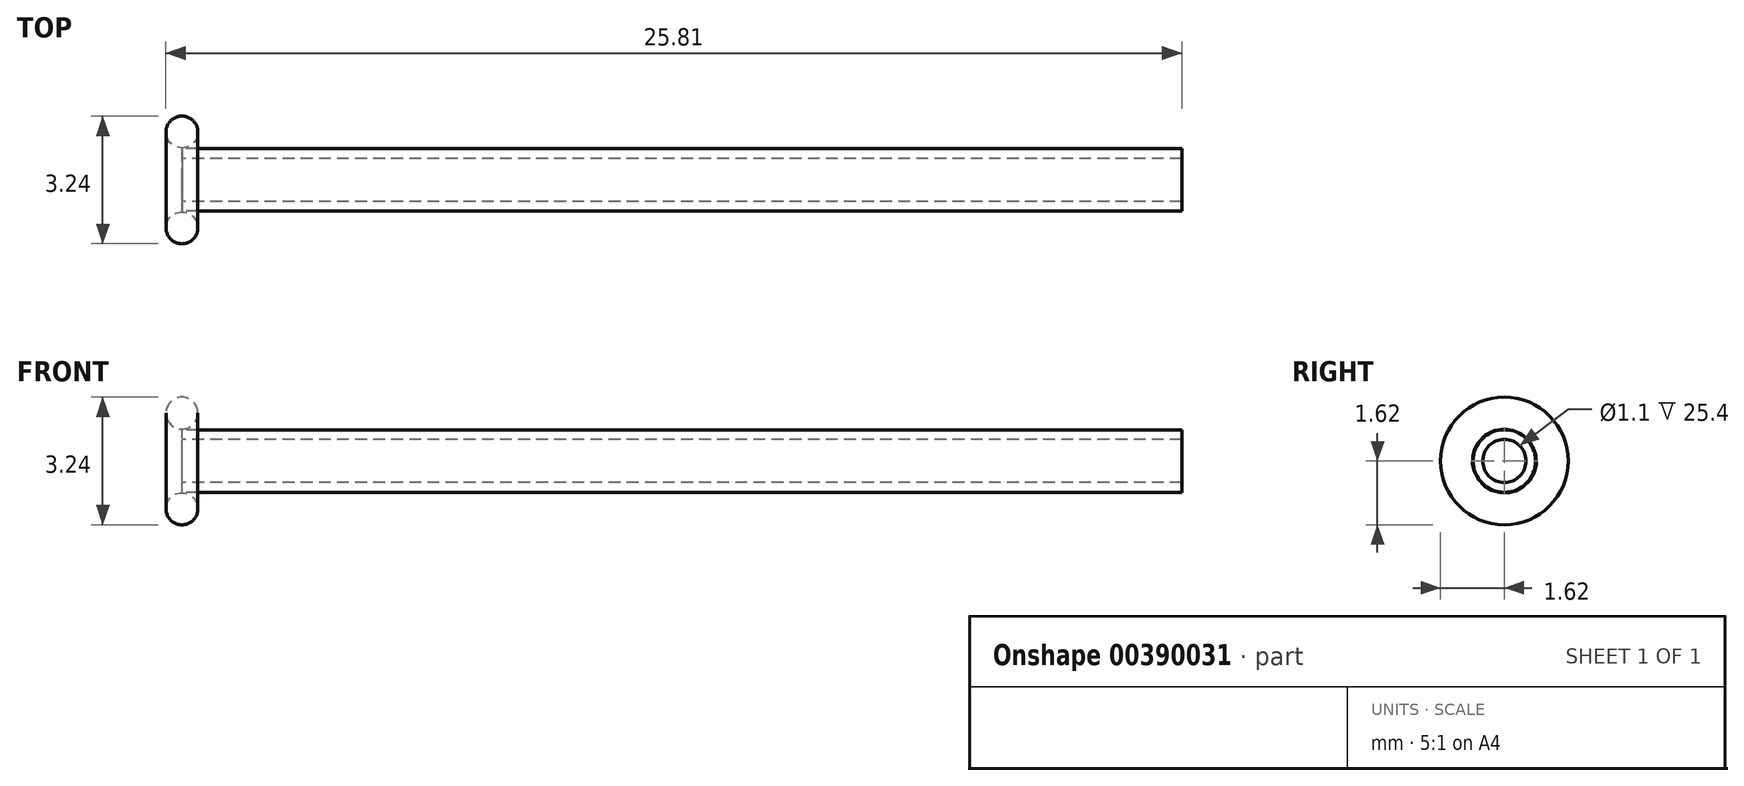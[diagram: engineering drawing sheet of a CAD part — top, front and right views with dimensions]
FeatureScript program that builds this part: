
annotation { "Feature Type Name" : "Feature", "Feature Type Description" : "" }
export const myFeature = defineFeature(function(context is Context, id is Id, definition is map)
    precondition{}
    {
        {
            var Q0;
            Q0=qCreatedBy(makeId("Right.planeOp"),FACE);
            var sketch = newSketch(context, id + "F0", { "sketchPlane" : qUnion([Q0])});
            skCircle(sketch, "E0", {"center": v(0, 0) * mm, "radius": 0.8 * mm});
            skCircle(sketch, "E1", {"center": v(0, 0) * mm, "radius": 0.55 * mm});
            skSolve(sketch);
        }
        {
            var Q0;
            Q0=makeQuery(id+"F0.imprint","IMPRINT",FACE,{"disambiguationData":[TD([[makeQuery(id+"F0.imprint","IMPRINT",EDGE,{"derivedFrom":sQuery(id+"F0.wireOp",EDGE,"E0")}),1.0]])]});
            extrude(context, id + "F1", {"entities" : qUnion([Q0]), "depth" : 25.4 * mm});
        }
        {
            var Q0;
            Q0=qCreatedBy(makeId("Front.planeOp"),FACE);
            var sketch = newSketch(context, id + "F2", { "sketchPlane" : qUnion([Q0])});
            skLineSegment(sketch, "E2", {"start": v(0, 0) * mm, "end": v(25.42, 0) * mm, "construction": true});
            skCircle(sketch, "E3", {"center": v(0, -1.22) * mm, "radius": 0.4 * mm});
            skSolve(sketch);
        }
        {
            var Q0;
            Q0 = qSketchRegion(id + "F2", true);
            var Q1;
            Q1=sQuery(id+"F2.wireOp",EDGE,"E2");
            revolve(context, id + "F3", {"entities" : qUnion([Q0]), "axis" : qUnion([Q1]), "revolveType" : RevolveType.FULL});
        }
    });
